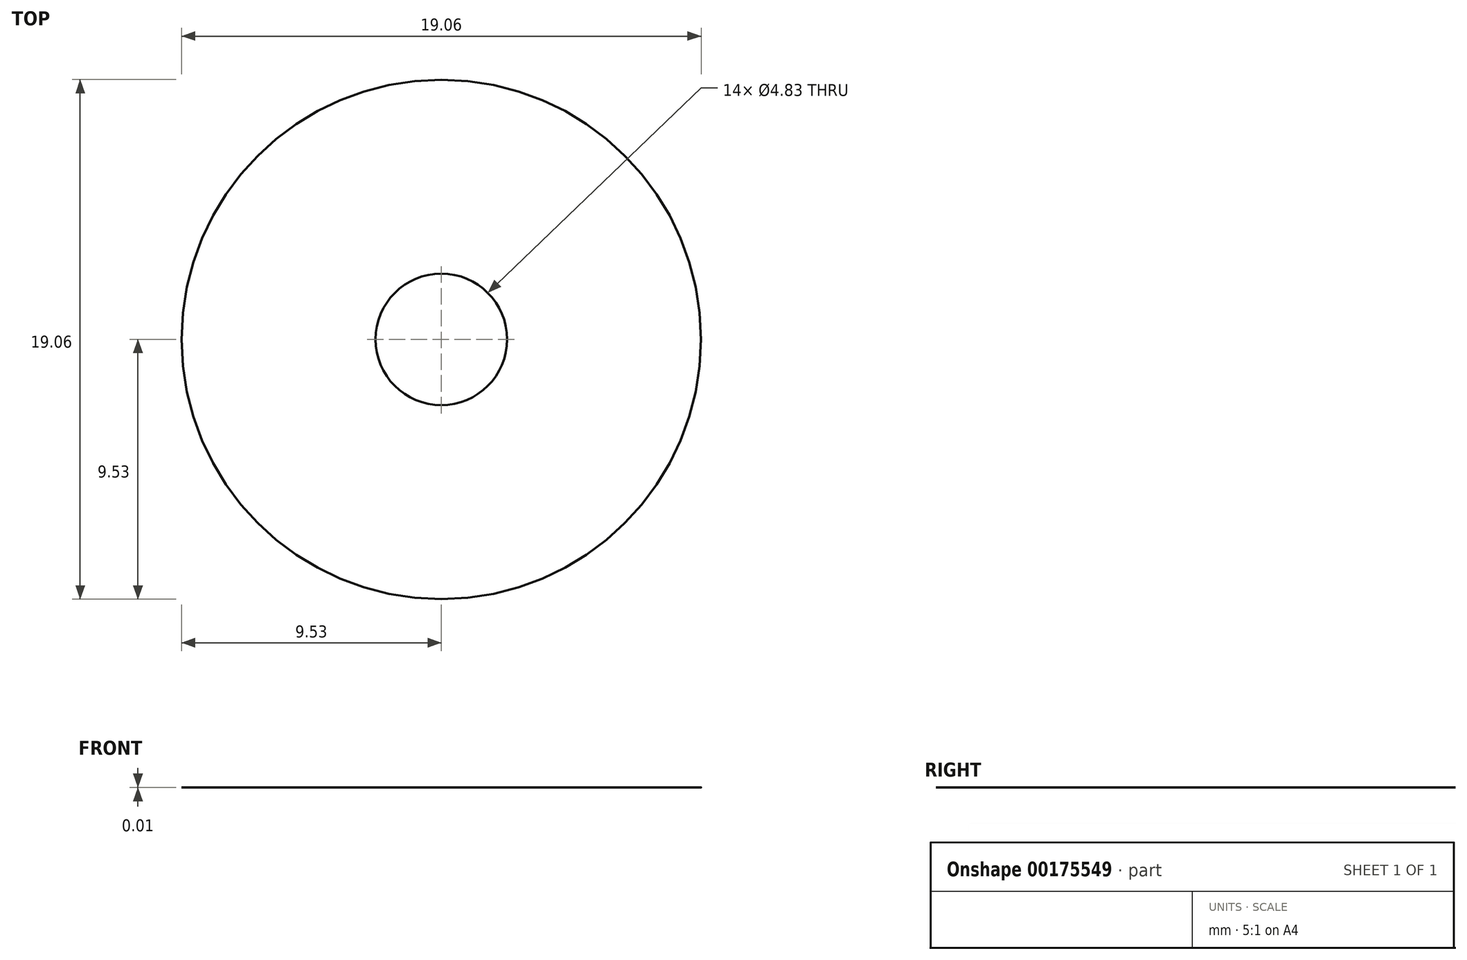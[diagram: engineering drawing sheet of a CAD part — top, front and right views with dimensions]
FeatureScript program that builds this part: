
annotation { "Feature Type Name" : "Feature", "Feature Type Description" : "" }
export const myFeature = defineFeature(function(context is Context, id is Id, definition is map)
    precondition{}
    {
        {
            var Q0;
            Q0=qCreatedBy(makeId("Top.planeOp"),FACE);
            var sketch = newSketch(context, id + "F0", { "sketchPlane" : qUnion([Q0])});
            skCircle(sketch, "E0", {"center": v(0, 0) * mm, "radius": 9.53 * mm});
            skCircle(sketch, "E1", {"center": v(0, 0) * mm, "radius": 2.41 * mm});
            skSolve(sketch);
        }
        {
            var Q0;
            Q0=makeQuery(id+"F0.imprint","IMPRINT",FACE,{"disambiguationData":[TD([[makeQuery(id+"F0.imprint","IMPRINT",EDGE,{"derivedFrom":sQuery(id+"F0.wireOp",EDGE,"E0")}),1.0]])]});
            extrude(context, id + "F1", {"entities" : qUnion([Q0]), "depth" : 1 / 101.6 * mm});
        }
    });
